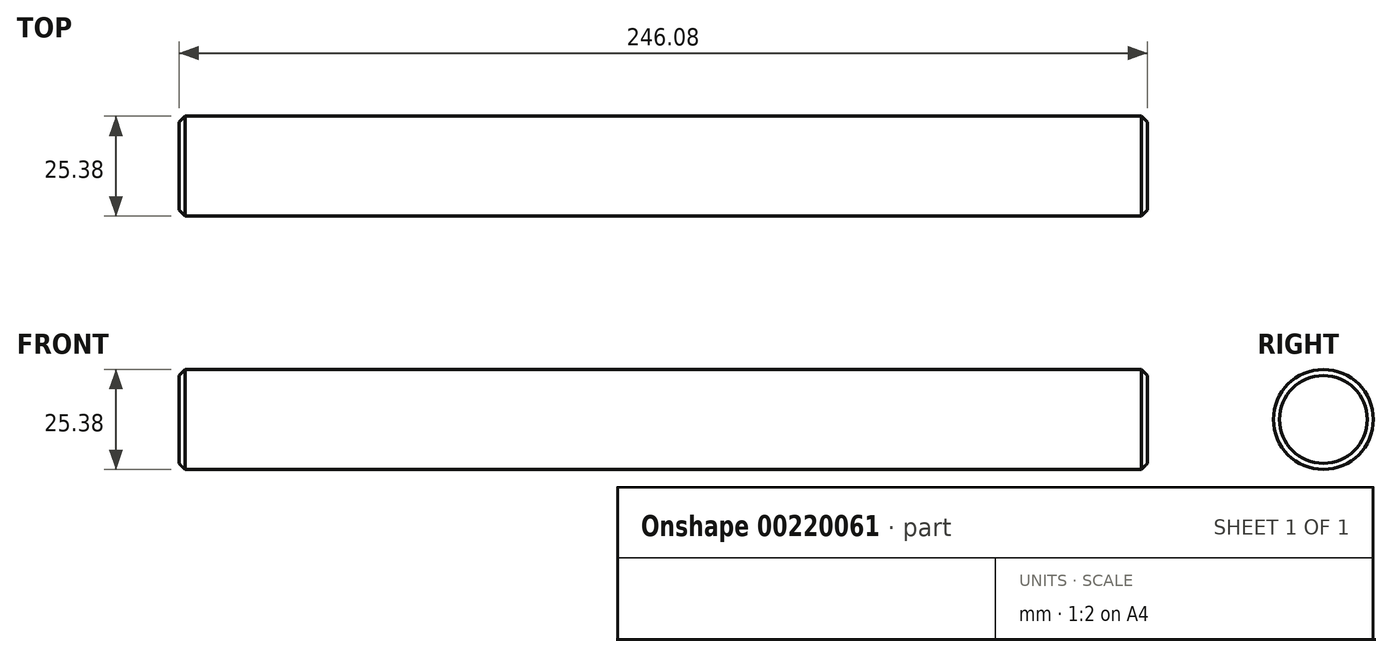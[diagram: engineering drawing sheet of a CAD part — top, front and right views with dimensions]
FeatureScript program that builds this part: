
annotation { "Feature Type Name" : "Feature", "Feature Type Description" : "" }
export const myFeature = defineFeature(function(context is Context, id is Id, definition is map)
    precondition{}
    {
        {
            var Q0;
            Q0=qCreatedBy(makeId("Right.planeOp"),FACE);
            var sketch = newSketch(context, id + "F0", { "sketchPlane" : qUnion([Q0])});
            skCircle(sketch, "E0", {"center": v(0, 0) * mm, "radius": 12.69 * mm});
            skSolve(sketch);
        }
        {
            var Q0;
            Q0 = qSketchRegion(id + "F0", true);
            extrude(context, id + "F1", {"entities" : qUnion([Q0]), "oppositeDirection" : true, "depth" : 246.08 * mm});
        }
        {
            var Q0;
            Q0=makeQuery(id+"F1.opExtrude","CAP_EDGE",EDGE,{"disambiguationData":[OSD([sQuery(id+"F0.wireOp",EDGE,"E0")])],"isStart":true});
            var Q1;
            Q1=makeQuery(id+"F1.opExtrude","CAP_EDGE",EDGE,{"disambiguationData":[OSD([sQuery(id+"F0.wireOp",EDGE,"E0")])],"isStart":false});
            chamfer(context, id + "F2", {"entities" : qUnion([Q0, Q1]), "width" : 1.52 * mm, "tangentPropagation" : true});
        }
    });
